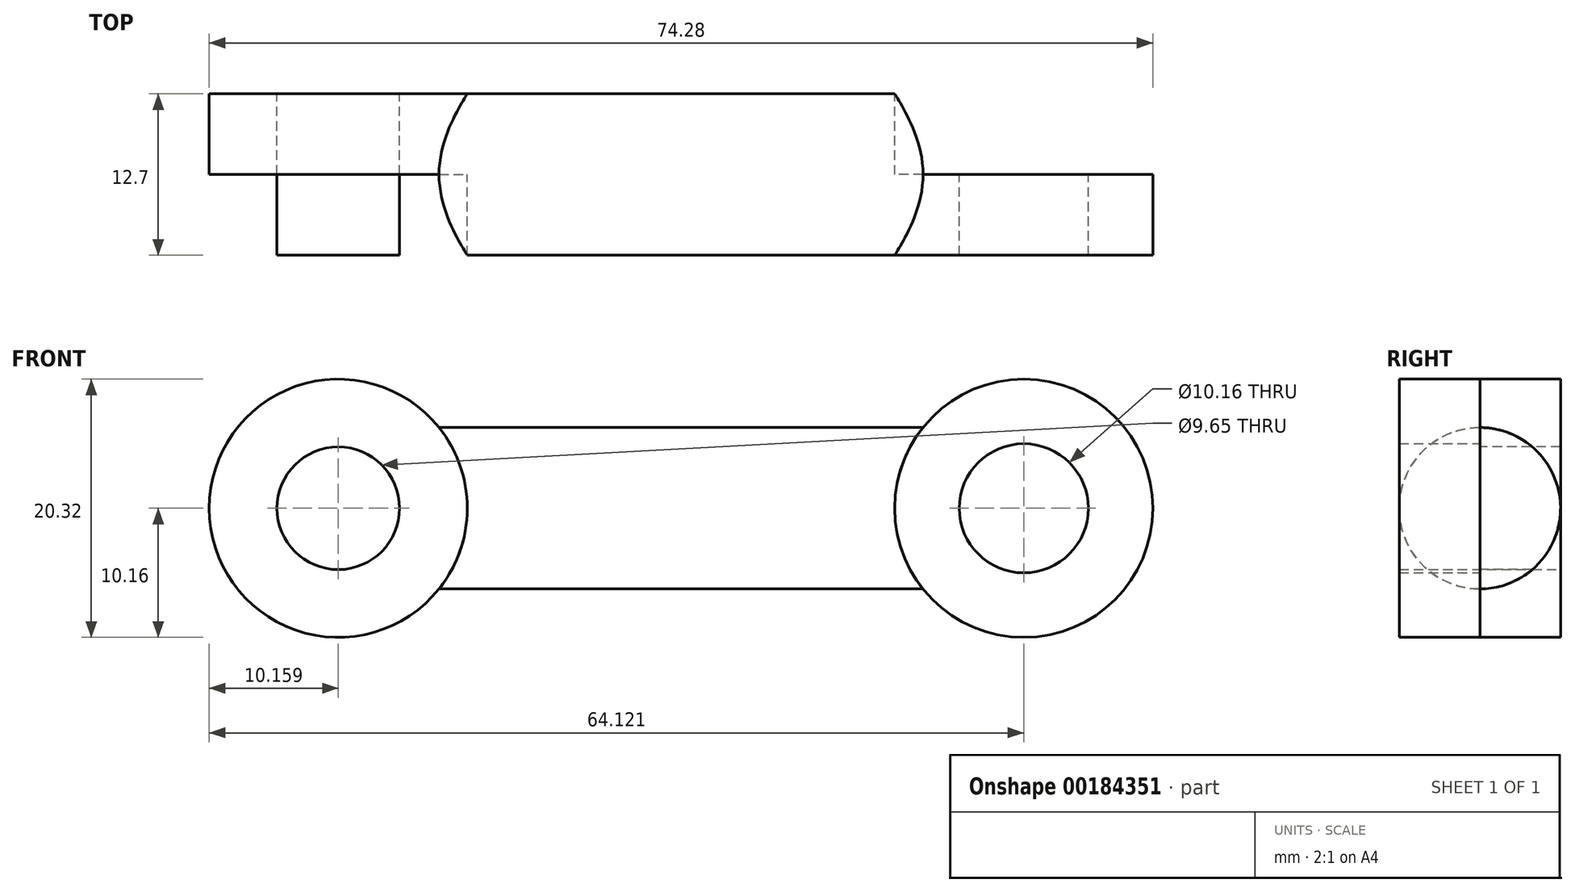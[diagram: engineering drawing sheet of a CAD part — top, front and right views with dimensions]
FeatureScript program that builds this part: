
annotation { "Feature Type Name" : "Feature", "Feature Type Description" : "" }
export const myFeature = defineFeature(function(context is Context, id is Id, definition is map)
    precondition{}
    {
        {
            var Q0;
            Q0=qCreatedBy(makeId("Front.planeOp"),FACE);
            var sketch = newSketch(context, id + "F0", { "sketchPlane" : qUnion([Q0])});
            skLineSegment(sketch, "E0.bottom", {"start": v(-19.05, 6.35) * mm, "end": v(19.05, 6.35) * mm});
            skLineSegment(sketch, "E0.top", {"start": v(-19.05, -6.35) * mm, "end": v(19.05, -6.35) * mm});
            skLineSegment(sketch, "E0.left", {"start": v(-19.05, 6.35) * mm, "end": v(-19.05, -6.35) * mm});
            skLineSegment(sketch, "E0.right", {"start": v(19.05, 6.35) * mm, "end": v(19.05, -6.35) * mm});
            skPoint(sketch, "E0.middle", {"position": v(0, 0) * mm});
            skCircle(sketch, "E1", {"center": v(26.98, 0) * mm, "radius": 10.16 * mm});
            skPoint(sketch, "E1.third.point", {"position": v(37.14, 0) * mm});
            skCircle(sketch, "E2", {"center": v(-26.98, 0) * mm, "radius": 10.16 * mm});
            skPoint(sketch, "E2.third.point", {"position": v(-37.14, 0) * mm});
            skPoint(sketch, "E2.third.point.positionSnap0", {"position": v(-19.05, 0) * mm});
            skCircle(sketch, "E3", {"center": v(26.98, 0) * mm, "radius": 5.08 * mm});
            skCircle(sketch, "E4", {"center": v(-26.98, 0) * mm, "radius": 4.83 * mm});
            skSolve(sketch);
        }
        {
            var Q0;
            {var subQ0=sQuery(id+"F0.wireOp",EDGE,"E0.bottom");Q0=makeQuery(id+"F0.imprint","IMPRINT",FACE,{"disambiguationData":[TD([[makeQuery(id+"F0.imprint","IMPRINT",EDGE,{"derivedFrom":subQ0}),-1.0]])]});}
            extrude(context, id + "F1", {"entities" : qUnion([Q0]), "endBound" : BoundingType.SYMMETRIC, "depth" : 12.7 * mm});
        }
        {
            var Q0;
            Q0=makeQuery(id+"F1.opExtrude","CAP_EDGE",EDGE,{"disambiguationData":[OSD([sQuery(id+"F0.wireOp",EDGE,"E0.bottom")])],"isStart":false});
            var Q1;
            Q1=makeQuery(id+"F1.opExtrude","CAP_EDGE",EDGE,{"disambiguationData":[OSD([sQuery(id+"F0.wireOp",EDGE,"E0.bottom")])],"isStart":true});
            var Q2;
            Q2=makeQuery(id+"F1.opExtrude","CAP_EDGE",EDGE,{"disambiguationData":[OSD([sQuery(id+"F0.wireOp",EDGE,"E0.top")])],"isStart":false});
            var Q3;
            Q3=makeQuery(id+"F1.opExtrude","CAP_EDGE",EDGE,{"disambiguationData":[OSD([sQuery(id+"F0.wireOp",EDGE,"E0.top")])],"isStart":true});
            fillet(context, id + "F2", {"entities" : qUnion([Q0, Q1, Q2, Q3]), "radius" : 6.35 * mm, "tangentPropagation" : true, "allowEdgeOverflow" : false});
        }
        {
            var Q0;
            {var subQ0=sQuery(id+"F0.wireOp",EDGE,"E0.right");Q0=makeQuery(id+"F0.imprint","IMPRINT",FACE,{"disambiguationData":[TD([[makeQuery(id+"F0.imprint","IMPRINT",EDGE,{"derivedFrom":subQ0}),1.0]])]});}
            var Q1;
            {var subQ0=sQuery(id+"F0.wireOp",EDGE,"E0.right");Q1=makeQuery(id+"F0.imprint","IMPRINT",FACE,{"disambiguationData":[TD([[makeQuery(id+"F0.imprint","IMPRINT",EDGE,{"derivedFrom":subQ0}),-1.0]])]});}
            extrude(context, id + "F3", {"entities" : qUnion([Q0, Q1]), "operationType" : NewBodyOperationType.ADD, "depth" : 6.35 * mm});
        }
        {
            var Q0;
            {var subQ0=sQuery(id+"F0.wireOp",EDGE,"E0.left");Q0=makeQuery(id+"F0.imprint","IMPRINT",FACE,{"disambiguationData":[TD([[makeQuery(id+"F0.imprint","IMPRINT",EDGE,{"derivedFrom":subQ0}),-1.0]])]});}
            var Q1;
            {var subQ0=sQuery(id+"F0.wireOp",EDGE,"E0.left");Q1=makeQuery(id+"F0.imprint","IMPRINT",FACE,{"disambiguationData":[TD([[makeQuery(id+"F0.imprint","IMPRINT",EDGE,{"derivedFrom":subQ0}),1.0]])]});}
            extrude(context, id + "F4", {"entities" : qUnion([Q0, Q1]), "operationType" : NewBodyOperationType.ADD, "oppositeDirection" : true, "depth" : 6.35 * mm});
        }
        {
            var Q0;
            Q0=makeQuery(id+"F0.imprint","IMPRINT",FACE,{"disambiguationData":[TD([[makeQuery(id+"F0.imprint","IMPRINT",EDGE,{"derivedFrom":sQuery(id+"F0.wireOp",EDGE,"E4")}),1.0]])]});
            extrude(context, id + "F5", {"entities" : qUnion([Q0]), "endBound" : BoundingType.SYMMETRIC, "depth" : 12.7 * mm});
        }
    });
